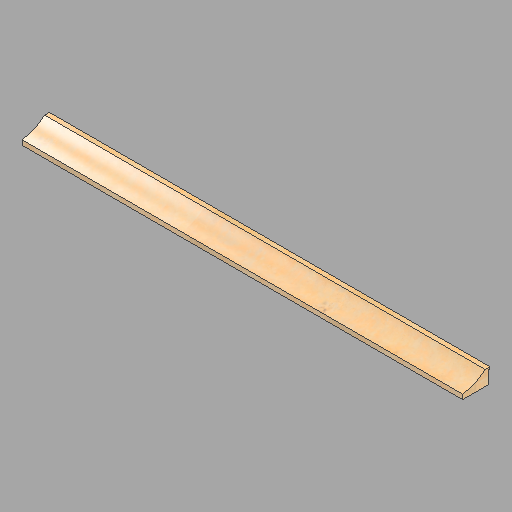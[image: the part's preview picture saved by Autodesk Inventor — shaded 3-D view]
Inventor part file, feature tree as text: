
AUTODESK INVENTOR PART (.ipt)
format: ipt  version: 2022.2 (Build 262287010, 287A)  size: 164,352 bytes
history: native  units: in
note: dims shown in document units (in); Inventor stores cm internally (conversion verified against a paired STEP export)
features: revolve x2, direct_edit x1, other x1
ambient origin geometry x8: Origin, YZ Plane, XZ Plane, XY Plane, X Axis, Y Axis, Z Axis, Center Point
bodies: Solid1 (feature_tree)
feature tree (4):
  direct_edit  "Direct Edit1"
  other  "Jamb (lower) (1)"
  revolve  "Rotate1"  [1 undecoded]
  revolve  "Rotate2"  [1 undecoded]
note: 2 required parameter values undecoded (feature->parameter linkage not recoverable at this tier; creation-order binding heuristic only, values carry confidence <= 0.55)
